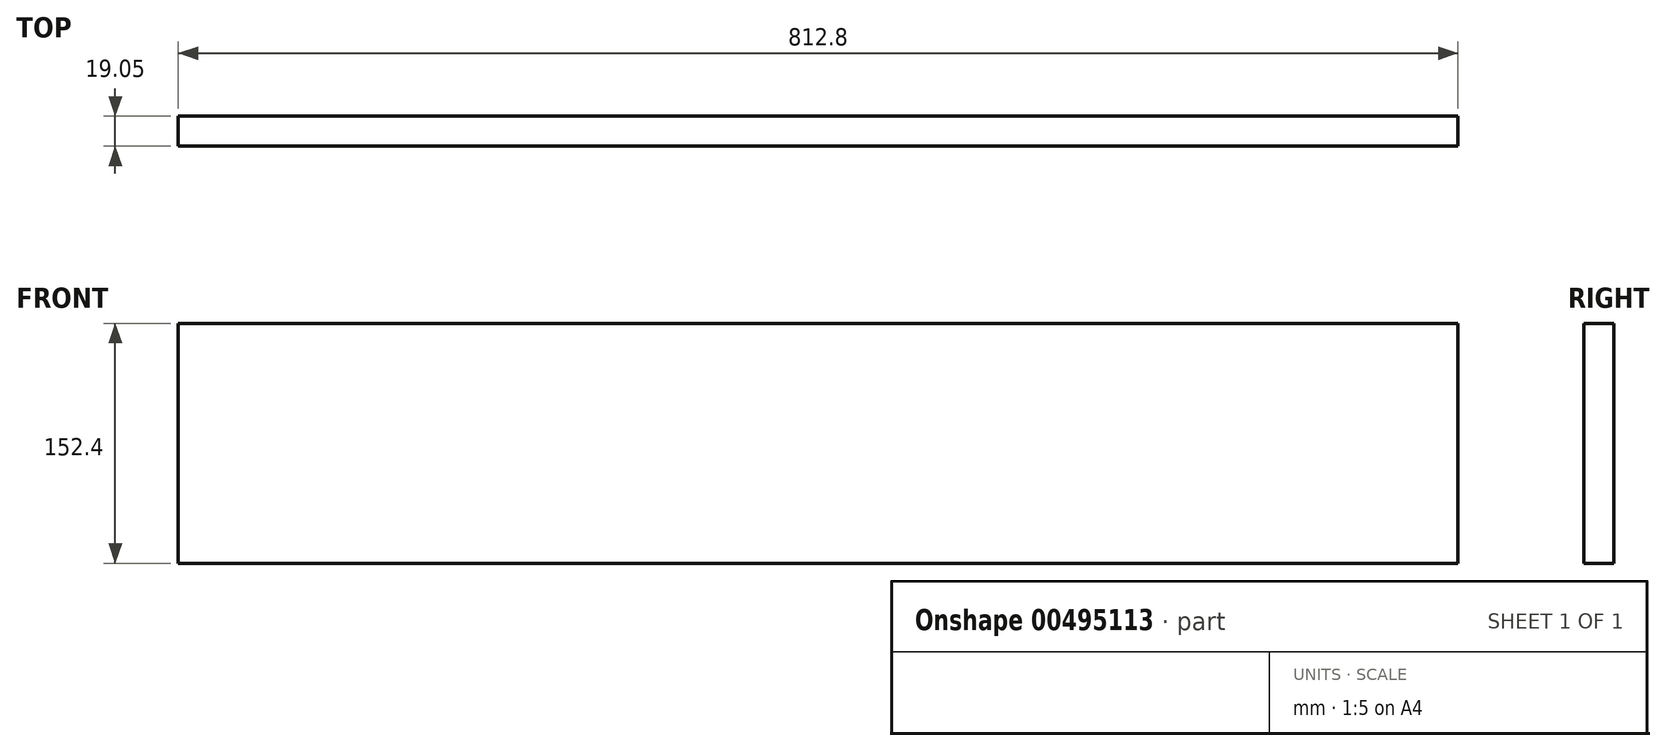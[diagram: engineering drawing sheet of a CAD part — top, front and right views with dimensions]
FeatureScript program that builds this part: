
annotation { "Feature Type Name" : "Feature", "Feature Type Description" : "" }
export const myFeature = defineFeature(function(context is Context, id is Id, definition is map)
    precondition{}
    {
        {
            var Q0;
            Q0=qCreatedBy(makeId("Front.planeOp"),FACE);
            var sketch = newSketch(context, id + "F0", { "sketchPlane" : qUnion([Q0])});
            skLineSegment(sketch, "E0.bottom", {"start": v(0, 0) * mm, "end": v(-812.8, 0) * mm});
            skLineSegment(sketch, "E0.top", {"start": v(0, 152.4) * mm, "end": v(-812.8, 152.4) * mm});
            skLineSegment(sketch, "E0.left", {"start": v(0, 0) * mm, "end": v(0, 152.4) * mm});
            skLineSegment(sketch, "E0.right", {"start": v(-812.8, 0) * mm, "end": v(-812.8, 152.4) * mm});
            skSolve(sketch);
        }
        {
            var Q0;
            Q0=makeQuery(id+"F0.imprint","IMPRINT",FACE,{"disambiguationData":[TD([[makeQuery(id+"F0.imprint","IMPRINT",EDGE,{"derivedFrom":sQuery(id+"F0.wireOp",EDGE,"E0.bottom")}),-1.0]])]});
            extrude(context, id + "F1", {"entities" : qUnion([Q0]), "depth" : 19.05 * mm});
        }
    });
